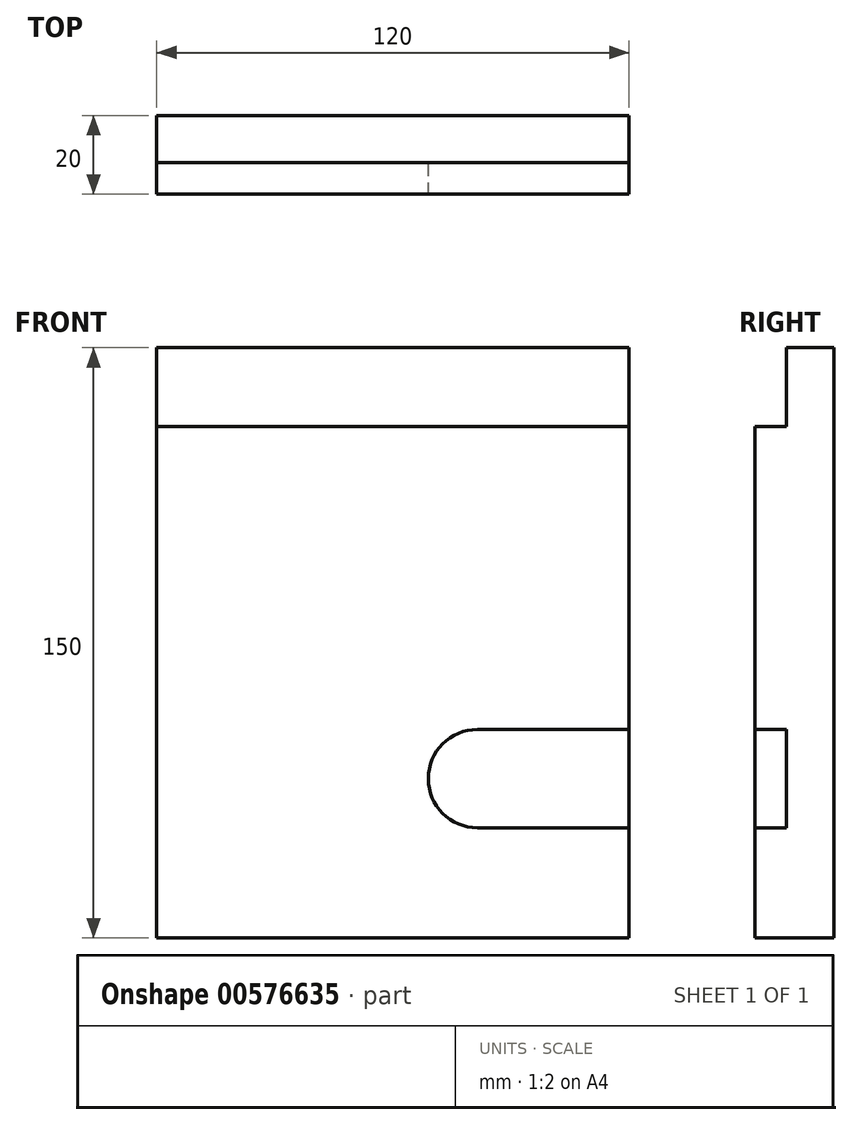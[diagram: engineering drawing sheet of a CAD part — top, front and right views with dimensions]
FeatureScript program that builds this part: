
annotation { "Feature Type Name" : "Feature", "Feature Type Description" : "" }
export const myFeature = defineFeature(function(context is Context, id is Id, definition is map)
    precondition{}
    {
        {
            var Q0;
            Q0=qCreatedBy(makeId("Front.planeOp"),FACE);
            var sketch = newSketch(context, id + "F0", { "sketchPlane" : qUnion([Q0])});
            skLineSegment(sketch, "E0", {"start": v(-120, 65.99) * mm, "end": v(-120, -84.01) * mm});
            skLineSegment(sketch, "E1", {"start": v(-120, -84.01) * mm, "end": v(0, -84.01) * mm});
            skLineSegment(sketch, "E2", {"start": v(-120, 65.99) * mm, "end": v(0, 65.99) * mm});
            skLineSegment(sketch, "E3", {"start": v(0, 65.99) * mm, "end": v(0, 45.99) * mm});
            skLineSegment(sketch, "E4", {"start": v(0, 45.99) * mm, "end": v(-120, 45.99) * mm});
            skLineSegment(sketch, "E5", {"start": v(0, 45.99) * mm, "end": v(0, -31.01) * mm});
            skLineSegment(sketch, "E6", {"start": v(0, -31.01) * mm, "end": v(0, -56.01) * mm});
            skLineSegment(sketch, "E7", {"start": v(0, -56.01) * mm, "end": v(0, -84.01) * mm});
            skLineSegment(sketch, "E8", {"start": v(-38.5, -31.01) * mm, "end": v(0, -31.01) * mm});
            skLineSegment(sketch, "E9", {"start": v(-38.5, -56.01) * mm, "end": v(0, -56.01) * mm});
            skLineSegment(sketch, "E10", {"start": v(-38.5, -31.01) * mm, "end": v(-120, -31.01) * mm});
            skLineSegment(sketch, "E11", {"start": v(-38.5, -56.01) * mm, "end": v(-120, -56.01) * mm});
            skArc(sketch, "E12", {"start": v(-38.5, -31.01) * mm, "mid": v(-51, -43.51) * mm, "end": v(-38.5, -56.01) * mm});
            skSolve(sketch);
        }
        {
            var Q0;
            {var subQ0=sQuery(id+"F0.wireOp",EDGE,"E2");Q0=makeQuery(id+"F0.imprint","IMPRINT",FACE,{"disambiguationData":[TD([[makeQuery(id+"F0.imprint","IMPRINT",EDGE,{"derivedFrom":subQ0}),-1.0]])]});}
            extrude(context, id + "F1", {"entities" : qUnion([Q0]), "depth" : 12 * mm, "offsetDistance" : 25 * mm});
        }
        {
            var Q0;
            {var subQ0=sQuery(id+"F0.wireOp",EDGE,"E4");Q0=makeQuery(id+"F0.imprint","IMPRINT",FACE,{"disambiguationData":[TD([[makeQuery(id+"F0.imprint","IMPRINT",EDGE,{"derivedFrom":subQ0}),1.0]])]});}
            extrude(context, id + "F2", {"entities" : qUnion([Q0]), "operationType" : NewBodyOperationType.ADD, "depth" : 20 * mm, "offsetDistance" : 25 * mm});
        }
        {
            var Q0;
            {var subQ0=sQuery(id+"F0.wireOp",EDGE,"E10");Q0=makeQuery(id+"F0.imprint","IMPRINT",FACE,{"disambiguationData":[TD([[makeQuery(id+"F0.imprint","IMPRINT",EDGE,{"derivedFrom":subQ0}),1.0]])]});}
            extrude(context, id + "F3", {"entities" : qUnion([Q0]), "operationType" : NewBodyOperationType.ADD, "depth" : 20 * mm, "offsetDistance" : 25 * mm});
        }
        {
            var Q0;
            {var subQ0=sQuery(id+"F0.wireOp",EDGE,"E1");Q0=makeQuery(id+"F0.imprint","IMPRINT",FACE,{"disambiguationData":[TD([[makeQuery(id+"F0.imprint","IMPRINT",EDGE,{"derivedFrom":subQ0}),1.0]])]});}
            extrude(context, id + "F4", {"entities" : qUnion([Q0]), "operationType" : NewBodyOperationType.ADD, "depth" : 20 * mm, "offsetDistance" : 25 * mm});
        }
        {
            var Q0;
            Q0=makeQuery(id+"F0.imprint","IMPRINT",FACE,{"disambiguationData":[TD([[makeQuery(id+"F0.imprint","IMPRINT",EDGE,{"derivedFrom":sQuery(id+"F0.wireOp",EDGE,"E6")}),-1.0]])]});
            extrude(context, id + "F5", {"entities" : qUnion([Q0]), "operationType" : NewBodyOperationType.ADD, "depth" : 12 * mm, "offsetDistance" : 25 * mm});
        }
    });
